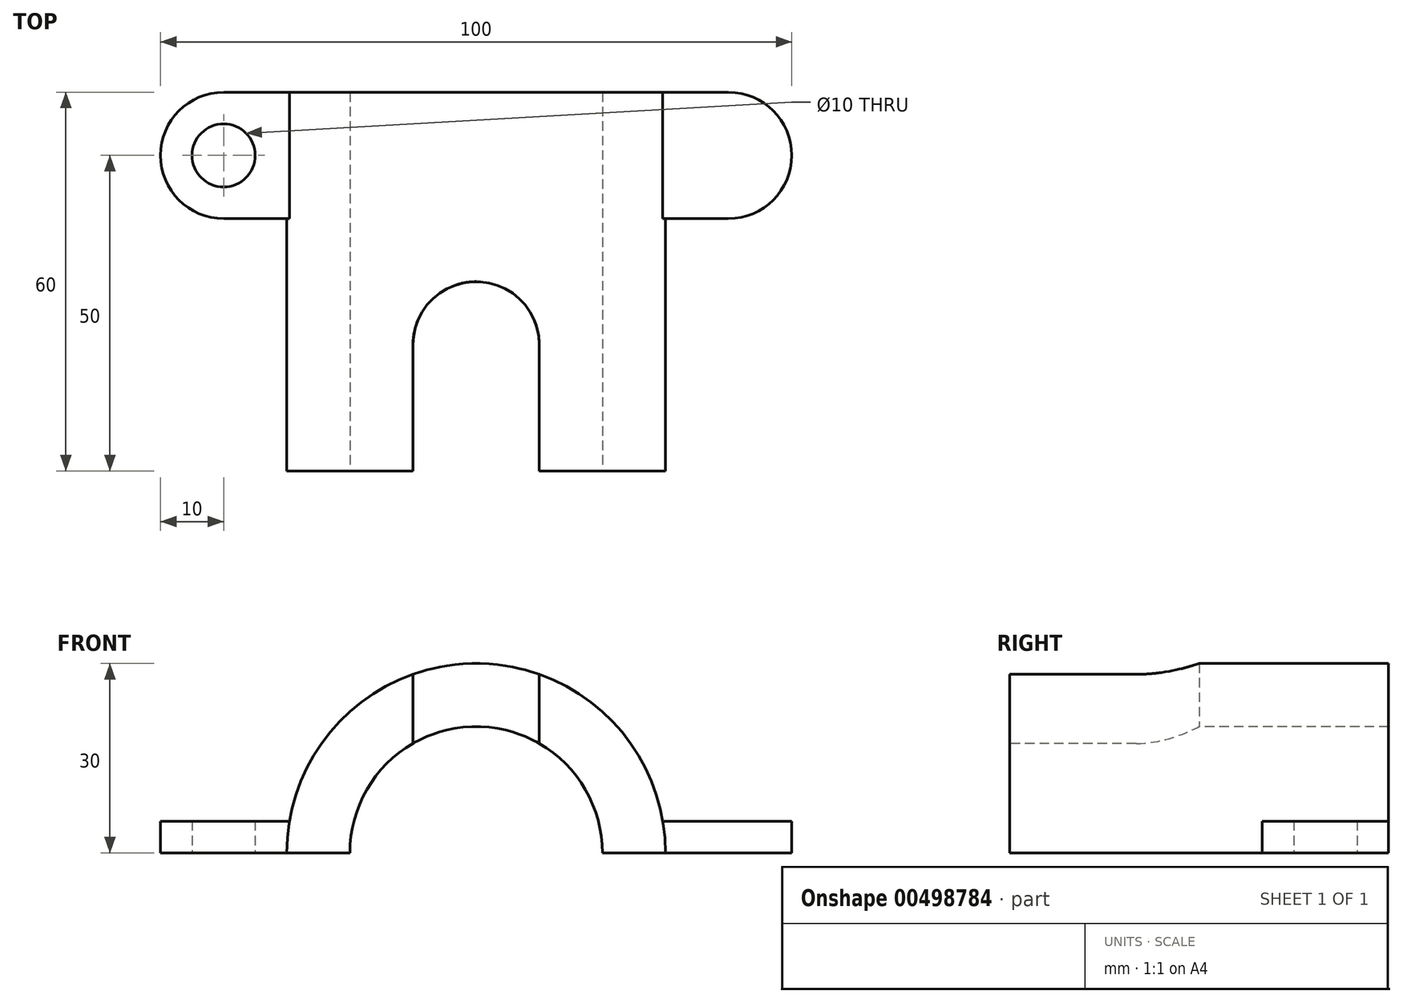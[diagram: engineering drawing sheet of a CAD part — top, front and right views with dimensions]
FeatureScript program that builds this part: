
annotation { "Feature Type Name" : "Feature", "Feature Type Description" : "" }
export const myFeature = defineFeature(function(context is Context, id is Id, definition is map)
    precondition{}
    {
        {
            assignVariable(context, id + "F0", {"name" : "a", "anyValue" : 5});
        }
        {
            var Q0;
            Q0=qCreatedBy(makeId("Front.planeOp"),FACE);
            var sketch = newSketch(context, id + "F1", { "sketchPlane" : qUnion([Q0])});
            skArc(sketch, "E0", {"start": v(30, 0) * mm, "mid": v(0, 30) * mm, "end": v(-30, 0) * mm});
            skLineSegment(sketch, "E1", {"start": v(-30, 0) * mm, "end": v(30, 0) * mm});
            skSolve(sketch);
        }
        {
            var Q0;
            Q0 = qSketchRegion(id + "F1", true);
            extrude(context, id + "F2", {"entities" : qUnion([Q0]), "oppositeDirection" : true, "depth" : 60 * mm});
        }
        {
            var Q0;
            Q0=qCreatedBy(makeId("Top.planeOp"),FACE);
            var sketch = newSketch(context, id + "F3", { "sketchPlane" : qUnion([Q0])});
            skLineSegment(sketch, "E2", {"start": v(-40, 50) * mm, "end": v(40, 50) * mm, "construction": true});
            skArc(sketch, "E3.0.startCap", {"start": v(-40, 40) * mm, "mid": v(-50, 50) * mm, "end": v(-40, 60) * mm});
            skArc(sketch, "E3.0.endCap", {"start": v(40, 60) * mm, "mid": v(50, 50) * mm, "end": v(40, 40) * mm});
            skLineSegment(sketch, "E3.0.left", {"start": v(-40, 60) * mm, "end": v(40, 60) * mm});
            skLineSegment(sketch, "E3.0.right", {"start": v(-40, 40) * mm, "end": v(40, 40) * mm});
            skPoint(sketch, "E4", {"position": v(0, 50) * mm});
            skSolve(sketch);
        }
        {
            var Q0;
            Q0 = qSketchRegion(id + "F3", true);
            extrude(context, id + "F4", {"entities" : qUnion([Q0]), "operationType" : NewBodyOperationType.ADD, "depth" : (getVariable(context, 'a')) * mm, "offsetDistance" : 25 * mm});
        }
        {
            var Q0;
            Q0=qCreatedBy(makeId("Top.planeOp"),FACE);
            var sketch = newSketch(context, id + "F5", { "sketchPlane" : qUnion([Q0])});
            skCircle(sketch, "E5", {"center": v(-40, 50) * mm, "radius": 5 * mm});
            skSolve(sketch);
        }
        {
            var Q0;
            Q0 = qSketchRegion(id + "F5", true);
            extrude(context, id + "F6", {"entities" : qUnion([Q0]), "operationType" : NewBodyOperationType.REMOVE, "endBound" : BoundingType.UP_TO_NEXT, "depth" : 25 * mm});
        }
        {
            var Q0;
            Q0=qCreatedBy(makeId("Top.planeOp"),FACE);
            var sketch = newSketch(context, id + "F7", { "sketchPlane" : qUnion([Q0])});
            skLineSegment(sketch, "E6", {"start": v(-10, 0) * mm, "end": v(-10, 20) * mm});
            skLineSegment(sketch, "E7", {"start": v(-10, 0) * mm, "end": v(0, 0) * mm});
            skLineSegment(sketch, "E8", {"start": v(0, 0) * mm, "end": v(0, 30) * mm});
            skArc(sketch, "E9", {"start": v(-10, 20) * mm, "mid": v(-7.07, 27.07) * mm, "end": v(0, 30) * mm});
            skLineSegment(sketch, "E10", {"start": v(0, 51.89) * mm, "end": v(0, -11.89) * mm, "construction": true});
            skArc(sketch, "E11.MirrorCS", {"start": v(10, 20) * mm, "mid": v(7.07, 27.07) * mm, "end": v(0, 30) * mm});
            skLineSegment(sketch, "E12.MirrorCS", {"start": v(10, 0) * mm, "end": v(10, 20) * mm});
            skLineSegment(sketch, "E13.MirrorCS", {"start": v(10, 0) * mm, "end": v(0, 0) * mm});
            skSolve(sketch);
        }
        {
            var Q0;
            Q0 = qSketchRegion(id + "F7", true);
            extrude(context, id + "F8", {"entities" : qUnion([Q0]), "operationType" : NewBodyOperationType.REMOVE, "endBound" : BoundingType.UP_TO_NEXT, "depth" : 25 * mm});
        }
        {
            var Q0;
            {var subQ0=sQuery(id+"F1.wireOp",EDGE,"E0");var subQ1=sQuery(id+"F1.wireOp",EDGE,"E1");Q0=makeQuery(id+"F8.boolean.opBoolean","SPLIT",FACE,{"disambiguationData":[TD([makeQuery(id+"F8.opExtrude","SWEPT_FACE",FACE,{"disambiguationData":[OSD([sQuery(id+"F7.wireOp",EDGE,"E6")])]})])],"derivedFrom":makeQuery(id+"F2.opExtrude","CAP_FACE",FACE,{"disambiguationData":[OSD([subQ0,subQ1])],"isStart":true})});}
            var sketch = newSketch(context, id + "F9", { "sketchPlane" : qUnion([Q0])});
            skCircle(sketch, "E14", {"center": v(0, 0) * mm, "radius": 20 * mm});
            skSolve(sketch);
        }
        {
            var Q0;
            Q0 = qSketchRegion(id + "F9", true);
            extrude(context, id + "F10", {"entities" : qUnion([Q0]), "operationType" : NewBodyOperationType.REMOVE, "endBound" : BoundingType.THROUGH_ALL, "oppositeDirection" : true, "depth" : 25 * mm});
        }
    });
